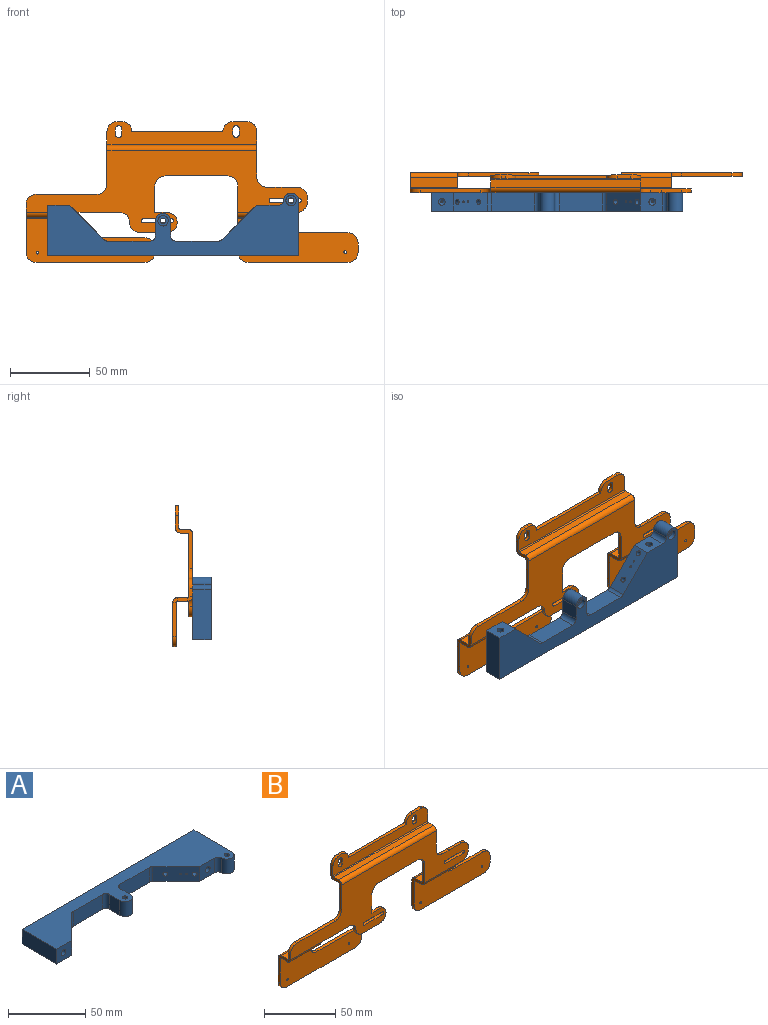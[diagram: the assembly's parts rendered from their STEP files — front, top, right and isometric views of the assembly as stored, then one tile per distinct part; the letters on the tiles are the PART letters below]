
ASSEMBLY  parts=2 mates=1
PART A: 70 faces, bbox 157.5x39.5x11.7 mm
  f0: plane 26.9x11.68mm, normal (0,-1,0), area 314.3mm2, adj f1,f61,f68,f69
  f1: cylinder r=3.17mm len=11.68mm, axis (0,0,1), area 29.1mm2, adj f0,f2,f61,f69
  f2: plane 21.52x21.52mm, normal (0.71,-0.71,0), area 336.5mm2, adj f1,f3,f53,f54,f57,f59,f61,f69
  f3: plane 13.79x11.68mm, normal (0,-1,0), area 147.3mm2, adj f2,f4,f47,f61,f69
  f4: plane 31.75x11.68mm, normal (-1,0,0), area 371mm2, adj f3,f5,f61,f69
  f5: plane 157.48x11.68mm, normal (0,1,0), area 1734.9mm2, adj f4,f6,f38,f46,f61,f69
  f6: plane 34.7x11.68mm, normal (1,0,0), area 405.4mm2, adj f5,f7,f61,f69
  f7: cylinder r=4.76mm len=11.68mm, axis (0,0,-1), area 173.2mm2, adj f6,f8,f61,f69
  f8: cylinder r=3.17mm len=11.68mm, axis (0,0,-1), area 57.2mm2, adj f7,f9,f61,f69
  f9: plane 13.79x11.68mm, normal (0,-1,0), area 147.3mm2, adj f8,f10,f37,f61,f69
  f10: plane 21.52x21.52mm, normal (-0.71,-0.71,0), area 336.5mm2, adj f9,f11,f17,f23,f33,f35,f61,f69
  f11: cylinder r=3.17mm len=11.68mm, axis (0,0,1), area 29.1mm2, adj f10,f12,f61,f69
  f12: plane 26.9x11.68mm, normal (0,-1,0), area 314.3mm2, adj f11,f13,f61,f69
  f13: cylinder r=3.17mm len=11.68mm, axis (0,0,-1), area 58.3mm2, adj f12,f14,f61,f69
  f14: plane 11.68x9.53mm, normal (1,0,0), area 111.3mm2, adj f13,f15,f61,f69
  f15: cylinder r=4.76mm len=11.68mm, axis (0,0,-1), area 174.8mm2, adj f14,f16,f61,f69
  f16: plane 11.68x9.53mm, normal (-1,0,0), area 111.3mm2, adj f15,f61,f68,f69
  f17: cylinder r=0.66mm len=14.4mm, axis (-0.71,-0.71,0), area 77.3mm2, adj f10,f18,f19,f20
  f18: cone r=0.66mm half-angle=60deg, axis (-0.71,-0.71,0), area 0mm2, adj f17,f20
  f19: cone r=0.66mm half-angle=60deg, axis (-0.71,-0.71,0), area 0mm2, adj f17,f20
  f20: cylinder r=0.66mm len=13.11mm, axis (0,-1,0), area 52.1mm2, adj f17,f18,f19,f21,f22
  f21: cone r=2.1mm half-angle=59deg, axis (0,-1,0), area 14.6mm2, adj f20,f37
  f22: cone r=0.66mm half-angle=60deg, axis (0,-1,0), area 1.6mm2, adj f20
  f23: cylinder r=0.66mm len=18mm, axis (-0.71,-0.71,0), area 99.4mm2, adj f10,f24,f30,f31,f32
  f24: cylinder r=0.41mm len=5.7mm, axis (0,1,0), area 13.7mm2, adj f23,f25,f30
  f25: cone r=0.41mm half-angle=45deg, axis (0,1,0), area 0.5mm2, adj f24,f26
  f26: plane 1.58x1.57mm, normal (0,1,0), area 1.1mm2, adj f25,f27
  f27: cone r=0.79mm half-angle=45deg, axis (0,-1,0), area 1mm2, adj f26,f28
  f28: cylinder r=0.91mm len=3.05mm, axis (0,1,0), area 17.5mm2, adj f27,f29
  f29: plane 8.18x8.18mm, normal (0,1,0), area 49.9mm2, adj f28,f46
  f30: cone r=0.66mm half-angle=60deg, axis (-0.71,-0.71,0), area 1.5mm2, adj f23,f24
  f31: cylinder r=0.41mm len=0.78mm, axis (0,1,0), area 0.1mm2, adj f23,f32
  f32: cone r=0.41mm half-angle=60deg, axis (0,1,0), area 0.1mm2, adj f23,f31
  f33: cylinder r=1.61mm len=5.65mm, axis (-0.71,-0.71,0), area 48.3mm2, adj f10,f34
  f34: cone r=1.61mm half-angle=60deg, axis (-0.71,-0.71,0), area 9.5mm2, adj f33
  f35: cylinder r=1.61mm len=5.65mm, axis (-0.71,-0.71,0), area 48.3mm2, adj f10,f36
  f36: cone r=1.61mm half-angle=60deg, axis (-0.71,-0.71,0), area 9.5mm2, adj f35
  f37: cylinder r=2.1mm len=6.35mm, axis (0,-1,0), area 83.8mm2, adj f9,f21
  f38: cylinder r=4.09mm len=8.18mm, axis (0,1,0), area 81.6mm2, adj f5,f39
  f39: plane 8.18x8.18mm, normal (0,1,0), area 49.9mm2, adj f38,f40
  f40: cylinder r=0.91mm len=3.05mm, axis (0,1,0), area 17.5mm2, adj f39,f41
  f41: cone r=0.79mm half-angle=45deg, axis (0,-1,0), area 1mm2, adj f40,f42
  f42: plane 1.57x1.57mm, normal (0,1,0), area 1.1mm2, adj f41,f43
  f43: cone r=0.41mm half-angle=45deg, axis (0,1,0), area 0.5mm2, adj f42,f44
  f44: cylinder r=0.41mm len=5.7mm, axis (0,1,0), area 13.7mm2, adj f43,f45,f54
  f45: cone r=0.66mm half-angle=60deg, axis (0.71,-0.71,0), area 1.5mm2, adj f44,f54
  f46: cylinder r=4.09mm len=8.18mm, axis (0,1,0), area 81.6mm2, adj f5,f29
  f47: cylinder r=2.1mm len=6.35mm, axis (0,-1,0), area 83.8mm2, adj f3,f48
  f48: cone r=2.1mm half-angle=59deg, axis (0,-1,0), area 14.6mm2, adj f47,f49
  f49: cylinder r=0.66mm len=13.11mm, axis (0,-1,0), area 52mm2, adj f48,f50,f51,f52,f53
  f50: cone r=0.66mm half-angle=60deg, axis (0.71,-0.71,0), area 0mm2, adj f49,f53
  f51: cone r=0.66mm half-angle=60deg, axis (0,-1,0), area 1.6mm2, adj f49
  f52: cone r=0.66mm half-angle=60deg, axis (0.71,-0.71,0), area 0mm2, adj f49,f53
  f53: cylinder r=0.66mm len=14.4mm, axis (0.71,-0.71,0), area 77.3mm2, adj f2,f49,f50,f52
  f54: cylinder r=0.66mm len=18mm, axis (0.71,-0.71,0), area 99.3mm2, adj f2,f44,f45,f55,f56
  f55: cylinder r=0.41mm len=0.78mm, axis (0,1,0), area 0mm2, adj f54,f56
  f56: cone r=0.41mm half-angle=60deg, axis (0,1,0), area 0.2mm2, adj f54,f55
  f57: cylinder r=1.61mm len=5.65mm, axis (0.71,-0.71,0), area 48.3mm2, adj f2,f58
  f58: cone r=1.61mm half-angle=60deg, axis (0.71,-0.71,0), area 9.5mm2, adj f57
  f59: cylinder r=1.61mm len=5.65mm, axis (0.71,-0.71,0), area 48.3mm2, adj f2,f60
  f60: cone r=1.61mm half-angle=60deg, axis (0.71,-0.71,0), area 9.5mm2, adj f59
  f61: plane 157.48x39.46mm, normal (0,0,1), area 3081.9mm2, adj f0,f1,f2,f3,f4,f5,f6,f7
  f62: cylinder r=1.7mm len=8.68mm, axis (0,0,-1), area 92.8mm2, adj f61,f63
  f63: plane 6.5x6.5mm, normal (0,0,-1), area 24.1mm2, adj f62,f64
  f64: cylinder r=3.25mm len=6.5mm, axis (0,0,-1), area 61.3mm2, adj f63,f69
  f65: cylinder r=1.7mm len=8.68mm, axis (0,0,-1), area 92.8mm2, adj f61,f66
  f66: plane 6.5x6.5mm, normal (0,0,-1), area 24.1mm2, adj f65,f67
  f67: cylinder r=3.25mm len=6.5mm, axis (0,0,-1), area 61.3mm2, adj f66,f69
  f68: cylinder r=3.17mm len=11.68mm, axis (0,0,-1), area 58.3mm2, adj f0,f16,f61,f69
  f69: plane 157.48x39.46mm, normal (0,0,-1), area 3033.6mm2, adj f0,f1,f2,f3,f4,f5,f6,f7
PART B: 99 faces, bbox 208.3x12.4x88.5 mm
  f0: plane 2.87x2.29mm, normal (0,0,1), area 6.6mm2, adj f10,f11,f60,f67
  f1: plane 30.07x6.4mm, normal (0,0,1), area 192.5mm2, adj f6,f9,f17,f51
  f2: plane 30.07x6.4mm, normal (0,0,-1), area 192.5mm2, adj f7,f8,f17,f51
  f3: plane 80.87x27.69mm, normal (0,1,0), area 1602.3mm2, adj f5,f6,f20,f48,f51,f52,f70,f71
  f4: plane 80.87x27.69mm, normal (0,-1,0), area 1602.3mm2, adj f5,f7,f20,f48,f51,f52,f70,f71
  f5: plane 68.17x2.29mm, normal (0,0,-1), area 155.8mm2, adj f3,f4,f70,f71
  f6: cylinder r=3.02mm len=30.07mm, axis (-1,0,0), area 142.8mm2, adj f1,f3,f25,f51
  f7: cylinder r=0.74mm len=30.07mm, axis (-1,0,0), area 34.8mm2, adj f2,f4,f25,f51
  f8: cylinder r=3.02mm len=30.07mm, axis (1,0,0), area 142.8mm2, adj f2,f15,f28,f51
  f9: cylinder r=0.74mm len=30.07mm, axis (1,0,0), area 34.8mm2, adj f1,f16,f28,f51
  f10: plane 93.98x14.25mm, normal (0,1,0), area 888.9mm2, adj f0,f33,f35,f36,f37,f38,f39,f40
  f11: plane 93.98x14.25mm, normal (0,-1,0), area 888.9mm2, adj f0,f34,f35,f36,f37,f38,f39,f40
  f12: plane 93.98x4.88mm, normal (0,0,1), area 458.3mm2, adj f31,f34,f44,f46
  f13: plane 93.98x4.88mm, normal (0,0,-1), area 458.3mm2, adj f32,f33,f44,f46
  f14: plane 4.98x2.29mm, normal (-1,0,0), area 11.4mm2, adj f15,f16,f28,f73
  f15: plane 176.53x51.74mm, normal (0,-1,0), area 3824.4mm2, adj f8,f14,f29,f31,f44,f45,f46,f47
  f16: plane 176.53x51.74mm, normal (0,1,0), area 3824.4mm2, adj f9,f14,f30,f32,f44,f45,f46,f47
  f17: plane 6.4x2.29mm, normal (-1,0,0), area 14.6mm2, adj f1,f2,f25,f28
  f18: plane 30.89x6.4mm, normal (0,0,1), area 197.7mm2, adj f26,f30,f50,f56
  f19: plane 30.89x6.4mm, normal (0,0,-1), area 197.7mm2, adj f27,f29,f50,f56
  f20: plane 21.34x2.29mm, normal (-1,0,0), area 48.8mm2, adj f3,f4,f25,f70
  f21: plane 75.34x27.69mm, normal (0,1,0), area 1662.5mm2, adj f23,f24,f26,f50,f55,f56,f62,f63
  f22: plane 75.34x27.69mm, normal (0,-1,0), area 1662.5mm2, adj f23,f24,f27,f50,f55,f56,f62,f63
  f23: plane 5.94x2.29mm, normal (1,0,0), area 13.6mm2, adj f21,f22,f62,f68
  f24: plane 62.64x2.29mm, normal (0,0,-1), area 143.2mm2, adj f21,f22,f68,f69
  f25: plane 3.02x3.02mm, normal (-1,0,0), area 6.7mm2, adj f6,f7,f17,f20
  f26: cylinder r=3.02mm len=30.89mm, axis (-1,0,0), area 146.6mm2, adj f18,f21,f50,f56
  f27: cylinder r=0.74mm len=30.89mm, axis (-1,0,0), area 35.7mm2, adj f19,f22,f50,f56
  f28: plane 3.02x3.02mm, normal (-1,0,0), area 6.7mm2, adj f8,f9,f14,f17
  f29: cylinder r=3.02mm len=30.89mm, axis (1,0,0), area 146.6mm2, adj f15,f19,f50,f56
  f30: cylinder r=0.74mm len=30.89mm, axis (1,0,0), area 35.7mm2, adj f16,f18,f50,f56
  f31: cylinder r=3.02mm len=93.98mm, axis (1,0,0), area 446.2mm2, adj f12,f15,f44,f46
  f32: cylinder r=0.74mm len=93.98mm, axis (1,0,0), area 108.7mm2, adj f13,f16,f44,f46
  f33: cylinder r=3.02mm len=93.98mm, axis (-1,0,0), area 446.2mm2, adj f10,f13,f44,f46
  f34: cylinder r=0.74mm len=93.98mm, axis (-1,0,0), area 108.7mm2, adj f11,f12,f44,f46
  f35: plane 8.56x2.29mm, normal (0,0,1), area 19.6mm2, adj f10,f11,f59,f66
  f36: cylinder r=2.03mm len=4.06mm, axis (0,1,0), area 14.6mm2, adj f10,f11,f37,f39
  f37: plane 3.3x2.29mm, normal (-1,0,0), area 7.5mm2, adj f10,f11,f36,f38
  f38: cylinder r=2.03mm len=4.06mm, axis (0,1,0), area 14.6mm2, adj f10,f11,f37,f39
  f39: plane 3.3x2.29mm, normal (1,0,0), area 7.5mm2, adj f10,f11,f36,f38
  f40: cylinder r=2.03mm len=4.06mm, axis (0,1,0), area 14.6mm2, adj f10,f11,f41,f43
  f41: plane 3.3x2.29mm, normal (-1,0,0), area 7.5mm2, adj f10,f11,f40,f42
  f42: cylinder r=2.03mm len=4.06mm, axis (0,1,0), area 14.6mm2, adj f10,f11,f41,f43
  f43: plane 3.3x2.29mm, normal (1,0,0), area 7.5mm2, adj f10,f11,f40,f42
  f44: plane 33.02x10.92mm, normal (-1,0,0), area 91.5mm2, adj f10,f11,f12,f13,f15,f16,f31,f32
  f45: plane 38.1x2.29mm, normal (0,0,1), area 87.1mm2, adj f15,f16,f73,f78
  f46: plane 28.58x10.92mm, normal (1,0,0), area 81.4mm2, adj f10,f11,f12,f13,f15,f16,f31,f32
  f47: plane 6.35x2.29mm, normal (0,0,1), area 14.5mm2, adj f15,f16,f61,f75
  f48: plane 2.87x2.29mm, normal (1,0,0), area 6.6mm2, adj f3,f4,f71,f72
  f49: plane 28.58x2.29mm, normal (0,0,-1), area 65.3mm2, adj f15,f16,f51,f65
  f50: plane 41.61x12.45mm, normal (-1,0,0), area 114.6mm2, adj f15,f16,f18,f19,f21,f22,f26,f27
  f51: plane 12.45x9.53mm, normal (1,0,0), area 41.3mm2, adj f1,f2,f3,f4,f6,f7,f8,f9
  f52: plane 38.1x2.29mm, normal (0,0,1), area 87.1mm2, adj f3,f4,f72,f74
  f53: plane 16.51x2.29mm, normal (1,0,0), area 37.7mm2, adj f15,f16,f77,f83
  f54: plane 39.37x2.29mm, normal (0,0,-1), area 90mm2, adj f15,f16,f76,f77
  f55: plane 31.75x2.29mm, normal (0,0,1), area 72.6mm2, adj f21,f22,f62,f63
  f56: plane 12.45x6.45mm, normal (1,0,0), area 34.3mm2, adj f18,f19,f21,f22,f26,f27,f29,f30
  f57: plane 17.15x2.29mm, normal (0,0,-1), area 39.2mm2, adj f15,f16,f64,f98
  f58: plane 57.15x2.29mm, normal (0,0,1), area 130.6mm2, adj f10,f11,f59,f60
  f59: cylinder r=6.35mm len=6.35mm, axis (0,-1,0), area 22.8mm2, adj f10,f11,f35,f58
  f60: cylinder r=6.35mm len=6.35mm, axis (0,-1,0), area 22.8mm2, adj f0,f10,f11,f58
  f61: cylinder r=6.35mm len=2.29mm, axis (0,1,0), area 1.3mm2, adj f15,f16,f47,f85
  f62: cylinder r=6.35mm len=6.35mm, axis (0,1,0), area 22.8mm2, adj f21,f22,f23,f55
  f63: cylinder r=6.35mm len=6.35mm, axis (0,1,0), area 22.8mm2, adj f21,f22,f55,f56
  f64: cylinder r=6.35mm len=6.35mm, axis (0,-1,0), area 22.8mm2, adj f15,f16,f57,f65
  f65: cylinder r=6.35mm len=6.35mm, axis (0,-1,0), area 22.8mm2, adj f15,f16,f49,f64
  f66: cylinder r=6.35mm len=6.35mm, axis (0,1,0), area 22.8mm2, adj f10,f11,f35,f46
  f67: cylinder r=6.35mm len=6.35mm, axis (0,-1,0), area 22.8mm2, adj f0,f10,f11,f44
  f68: cylinder r=6.35mm len=6.35mm, axis (0,-1,0), area 22.8mm2, adj f21,f22,f23,f24
  f69: cylinder r=6.35mm len=6.35mm, axis (0,1,0), area 22.8mm2, adj f21,f22,f24,f50
  f70: cylinder r=6.35mm len=6.35mm, axis (0,-1,0), area 22.8mm2, adj f3,f4,f5,f20
  f71: cylinder r=6.35mm len=6.35mm, axis (0,1,0), area 22.8mm2, adj f3,f4,f5,f48
  f72: cylinder r=6.35mm len=6.35mm, axis (0,-1,0), area 22.8mm2, adj f3,f4,f48,f52
  f73: cylinder r=6.35mm len=6.35mm, axis (0,-1,0), area 22.8mm2, adj f14,f15,f16,f45
  f74: cylinder r=6.35mm len=6.35mm, axis (0,1,0), area 22.8mm2, adj f3,f4,f51,f52
  f75: cylinder r=6.35mm len=6.35mm, axis (0,1,0), area 22.8mm2, adj f15,f16,f46,f47
  f76: cylinder r=6.35mm len=6.35mm, axis (0,1,0), area 22.8mm2, adj f15,f16,f50,f54
  f77: cylinder r=6.35mm len=6.35mm, axis (0,1,0), area 22.8mm2, adj f15,f16,f53,f54
  f78: cylinder r=6.35mm len=6.35mm, axis (0,1,0), area 22.8mm2, adj f15,f16,f44,f45
  f79: cylinder r=0.8mm len=2.29mm, axis (0,-1,0), area 11.5mm2, adj f21,f22
  f80: cylinder r=0.8mm len=2.29mm, axis (0,-1,0), area 11.5mm2, adj f21,f22
  f81: cylinder r=0.8mm len=2.29mm, axis (0,-1,0), area 11.5mm2, adj f3,f4
  f82: cylinder r=0.8mm len=2.29mm, axis (0,-1,0), area 11.5mm2, adj f3,f4
  f83: plane 7.62x2.29mm, normal (0,0,1), area 17.4mm2, adj f15,f16,f53,f97
  f84: plane 6.35x2.29mm, normal (0,0,-1), area 14.5mm2, adj f15,f16,f56,f95
  f85: plane 12.13x2.29mm, normal (0,0,1), area 27.7mm2, adj f15,f16,f61,f96
  f86: plane 3.05x2.29mm, normal (1,0,0), area 7mm2, adj f15,f16,f95,f96
  f87: cylinder r=1.27mm len=2.54mm, axis (0,-1,0), area 9.1mm2, adj f15,f16,f88,f90
  f88: plane 17.78x2.29mm, normal (0,0,-1), area 40.6mm2, adj f15,f16,f87,f89
  f89: cylinder r=1.27mm len=2.54mm, axis (0,-1,0), area 9.1mm2, adj f15,f16,f88,f90
  f90: plane 17.78x2.29mm, normal (0,0,1), area 40.6mm2, adj f15,f16,f87,f89
  f91: cylinder r=1.27mm len=2.54mm, axis (0,-1,0), area 9.1mm2, adj f15,f16,f92,f94
  f92: plane 17.78x2.29mm, normal (0,0,-1), area 40.6mm2, adj f15,f16,f91,f93
  f93: cylinder r=1.27mm len=2.54mm, axis (0,-1,0), area 9.1mm2, adj f15,f16,f92,f94
  f94: plane 17.78x2.29mm, normal (0,0,1), area 40.6mm2, adj f15,f16,f91,f93
  f95: cylinder r=6.35mm len=6.35mm, axis (0,-1,0), area 22.8mm2, adj f15,f16,f84,f86
  f96: cylinder r=6.35mm len=6.35mm, axis (0,-1,0), area 22.8mm2, adj f15,f16,f85,f86
  f97: cylinder r=6.35mm len=6.35mm, axis (0,-1,0), area 22.8mm2, adj f15,f16,f83,f98
  f98: cylinder r=6.35mm len=6.35mm, axis (0,-1,0), area 22.8mm2, adj f15,f16,f57,f97
PLACE A rot(axis=(-1,0,0),90deg) t=(12.51,-16.88,-39.82)mm
PLACE B t=(-102.66,4.96,-43.99)mm fixed
MATE pin_slot A.f15 <-> B.f87  axis (0,1,0) through (-16.7,-5.2,-17.82)mm
